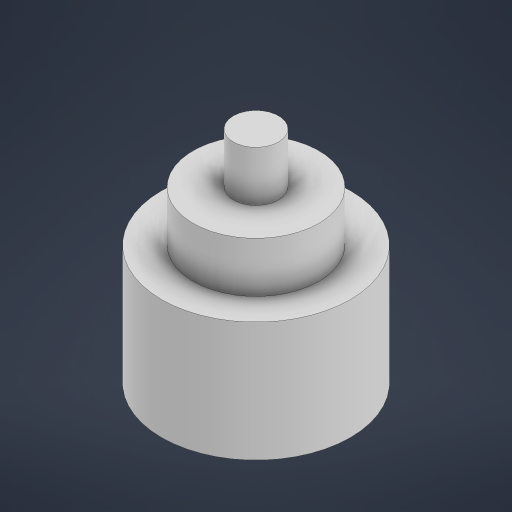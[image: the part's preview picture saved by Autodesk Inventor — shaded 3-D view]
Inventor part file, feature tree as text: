
AUTODESK INVENTOR PART (.ipt)
format: ipt  version: 2023 (Build 270158000, 158)  size: 203,776 bytes
history: native  units: in
note: dims shown in document units (in); Inventor stores cm internally (conversion verified against a paired STEP export)
features: extrude x4, sketch x3
ambient origin geometry x8: Origin, YZ Plane, XZ Plane, XY Plane, X Axis, Y Axis, Z Axis, Center Point
bodies: Solid1 (feature_tree)
feature tree (7):
  extrude  "Extrusion1"  Depth=1.378in TaperAngle=0.0deg
  sketch  "Sketch3"  dims[d3=0.2835in d4=0.7874in]
  extrude  "Extrusion2"  Depth=0.7874in
  extrude  "Extrusion3"  Depth=0.315in TaperAngle=0.0deg
  extrude  "Extrusion4"  Depth=0.2756in
  sketch  "Sketch2"  dims[d0=1.1811in d1=1.378in d2=0.0in]
  sketch  "Sketch4"  dims[d5=0.6299in d6=0.0in d7=0.315in d8=0.0in d9=0.3543in d10=0.2756in d11=0.0in]
